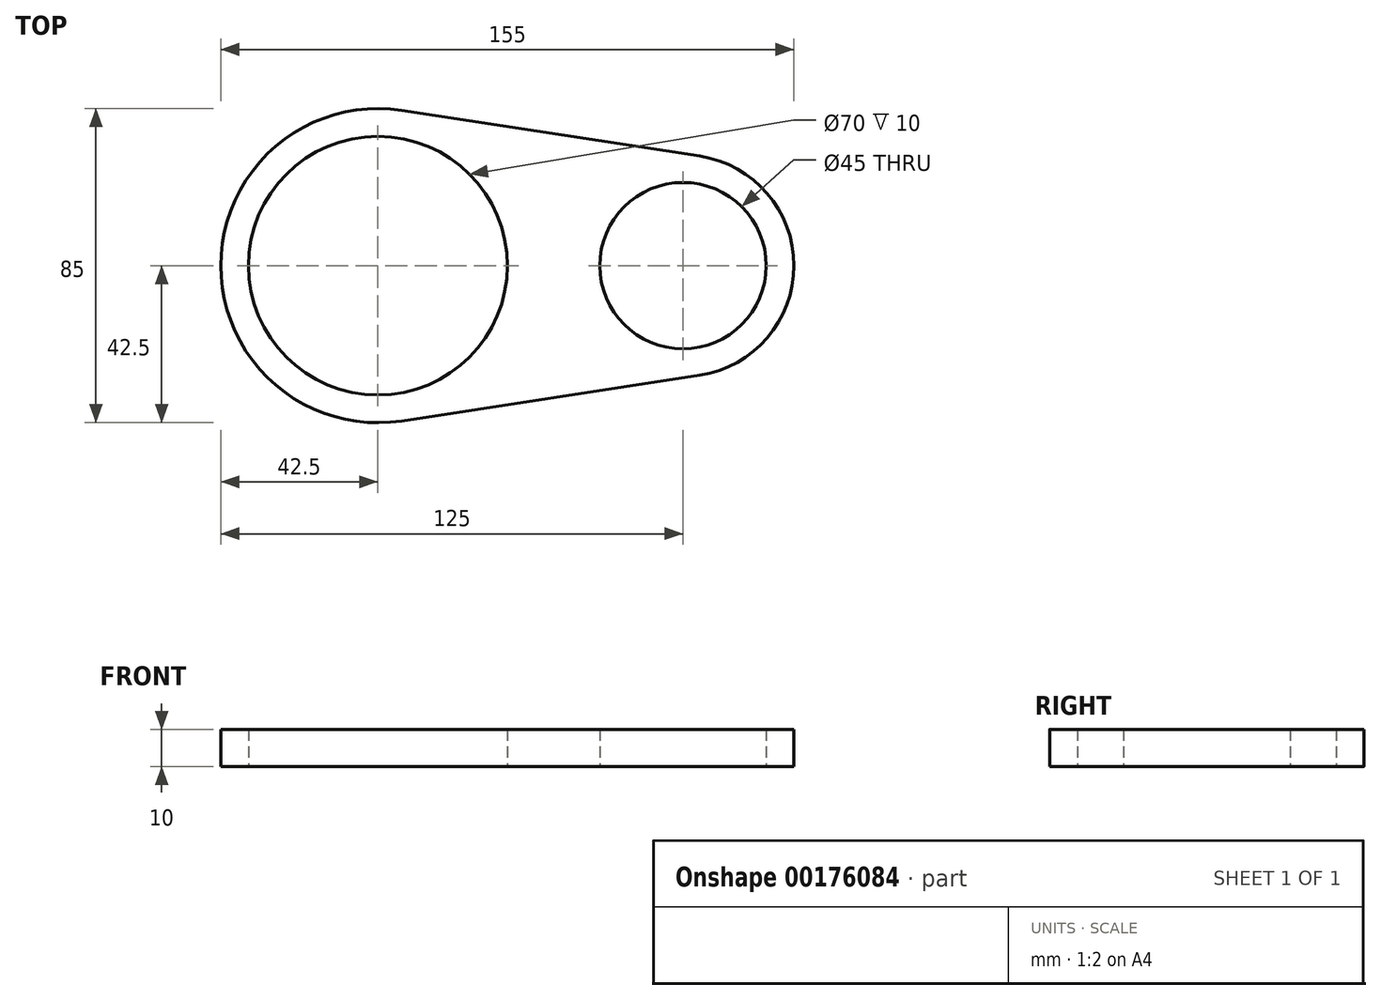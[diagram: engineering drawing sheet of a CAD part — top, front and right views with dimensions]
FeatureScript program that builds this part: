
annotation { "Feature Type Name" : "Feature", "Feature Type Description" : "" }
export const myFeature = defineFeature(function(context is Context, id is Id, definition is map)
    precondition{}
    {
        {
            var Q0;
            Q0=qCreatedBy(makeId("Top.planeOp"),FACE);
            var sketch = newSketch(context, id + "F0", { "sketchPlane" : qUnion([Q0])});
            skCircle(sketch, "E0", {"center": v(0, 0) * mm, "radius": 35 * mm});
            skArc(sketch, "E1", {"start": v(6.44, 42) * mm, "mid": v(-42.5, 0) * mm, "end": v(6.44, -42) * mm});
            skCircle(sketch, "E2", {"center": v(82.5, 0) * mm, "radius": 22.5 * mm});
            skArc(sketch, "E3", {"start": v(87.05, -29.65) * mm, "mid": v(112.5, 0) * mm, "end": v(87.05, 29.65) * mm});
            skLineSegment(sketch, "E4", {"start": v(6.44, 42) * mm, "end": v(87.05, 29.65) * mm});
            skLineSegment(sketch, "E5", {"start": v(6.44, -42) * mm, "end": v(87.05, -29.65) * mm});
            skSolve(sketch);
        }
        {
            var Q0;
            Q0=makeQuery(id+"F0.imprint","IMPRINT",FACE,{"disambiguationData":[TD([[makeQuery(id+"F0.imprint","IMPRINT",EDGE,{"derivedFrom":sQuery(id+"F0.wireOp",EDGE,"E0")}),-1.0]])]});
            extrude(context, id + "F1", {"entities" : qUnion([Q0]), "depth" : 10 * mm});
        }
    });
